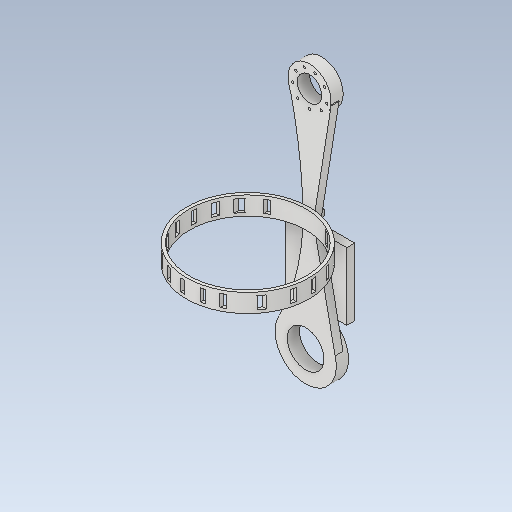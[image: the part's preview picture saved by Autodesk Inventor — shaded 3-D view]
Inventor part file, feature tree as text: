
AUTODESK INVENTOR PART (.ipt)
format: ipt  version: 2021 (Build 250183000, 183)  size: 348,160 bytes
history: native  units: in
note: dims shown in document units (in); Inventor stores cm internally (conversion verified against a paired STEP export)
features: sketch x19, extrude x13, plane x1
ambient origin geometry x8: Origin, YZ Plane, XZ Plane, XY Plane, X Axis, Y Axis, Z Axis, Center Point
bodies: Solid1 (feature_tree), Solid2 (feature_tree)
feature tree (33):
  extrude  "Extrusion1"  Depth=7.0866in
  extrude  "Extrusion2"  Depth=1.9685in
  extrude  "Extrusion3"  Depth=0.7874in TaperAngle=0.0deg
  extrude  "Extrusion4"  Depth=3.937in
  extrude  "Extrusion5"  Depth=0.5118in TaperAngle=0.0deg
  extrude  "Extrusion6"  Depth=0.3937in
  sketch  "Sketch7"  dims[d40=0.0787in d41=0.0in d43=1.1811in d44=0.0in]
  extrude  "Extrusion7"  Depth=1.1811in TaperAngle=0.0deg
  extrude  "Extrusion8"  Depth=1.1811in TaperAngle=0.0deg
  extrude  "Extrusion9"  Depth=0.5118in TaperAngle=0.0deg
  extrude  "Extrusion10"  Depth=0.1575in
  extrude  "Extrusion11"  Depth=0.1575in
  sketch  "Sketch13"  dims[d73=1.1811in d74=1.1811in]
  sketch  "Sketch14"  dims[d75=1.1811in]
  sketch  "Sketch15"  dims[d76=1.1811in]
  plane  "Work Plane1"
  extrude  "Extrusion12"  TaperAngle=0.0deg  [1 undecoded]
  sketch  "Sketch17"  dims[d78=1.1811in]
  sketch  "Sketch18"  dims[d79=1.1811in]
  extrude  "Extrusion13"  Depth=1.1811in
  sketch  "Sketch1"  dims[d9=2.7559in d12=7.0866in]
  sketch  "Sketch2"  dims[d13=7.0866in d14=1.9685in]
  sketch  "Sketch3"  dims[d15=0.5118in d16=0.0in d22=0.7874in d23=0.5118in d24=0.0in d25=0.0in]
  sketch  "Sketch4"  dims[d28=0.7874in d29=0.5118in d30=0.0in d31=0.0in d32=3.937in]
  sketch  "Sketch5"  dims[d33=4.3307in d34=0.5118in d35=0.0in]
  sketch  "Sketch6"  dims[d37=0.2756in d38=0.0in d39=0.3937in]
  sketch  "Sketch8"  dims[d45=7.4803in d46=1.1811in d47=0.0in]
  sketch  "Sketch9"  dims[d48=0.5118in d49=0.0in d50=0.5118in d51=0.0in]
  sketch  "Sketch10"  dims[d54=0.1575in d67=0.1575in]
  sketch  "Sketch11"  dims[d68=0.1575in d69=0.1575in]
  sketch  "Sketch12"  dims[d70=0.7874in d71=0.0in d72=0.0in]
  sketch  "Sketch16"  dims[d77=1.1811in]
  sketch  "Sketch19"  dims[d80=1.1811in d81=1.1811in d82=1.1811in d83=1.1811in d84=1.1811in d85=1.1811in d86=0.7874in d87=0.0in d88=7.874in d106=0.7874in d107=0.0in]
note: 1 required parameter value undecoded (feature->parameter linkage not recoverable at this tier; creation-order binding heuristic only, values carry confidence <= 0.55)
